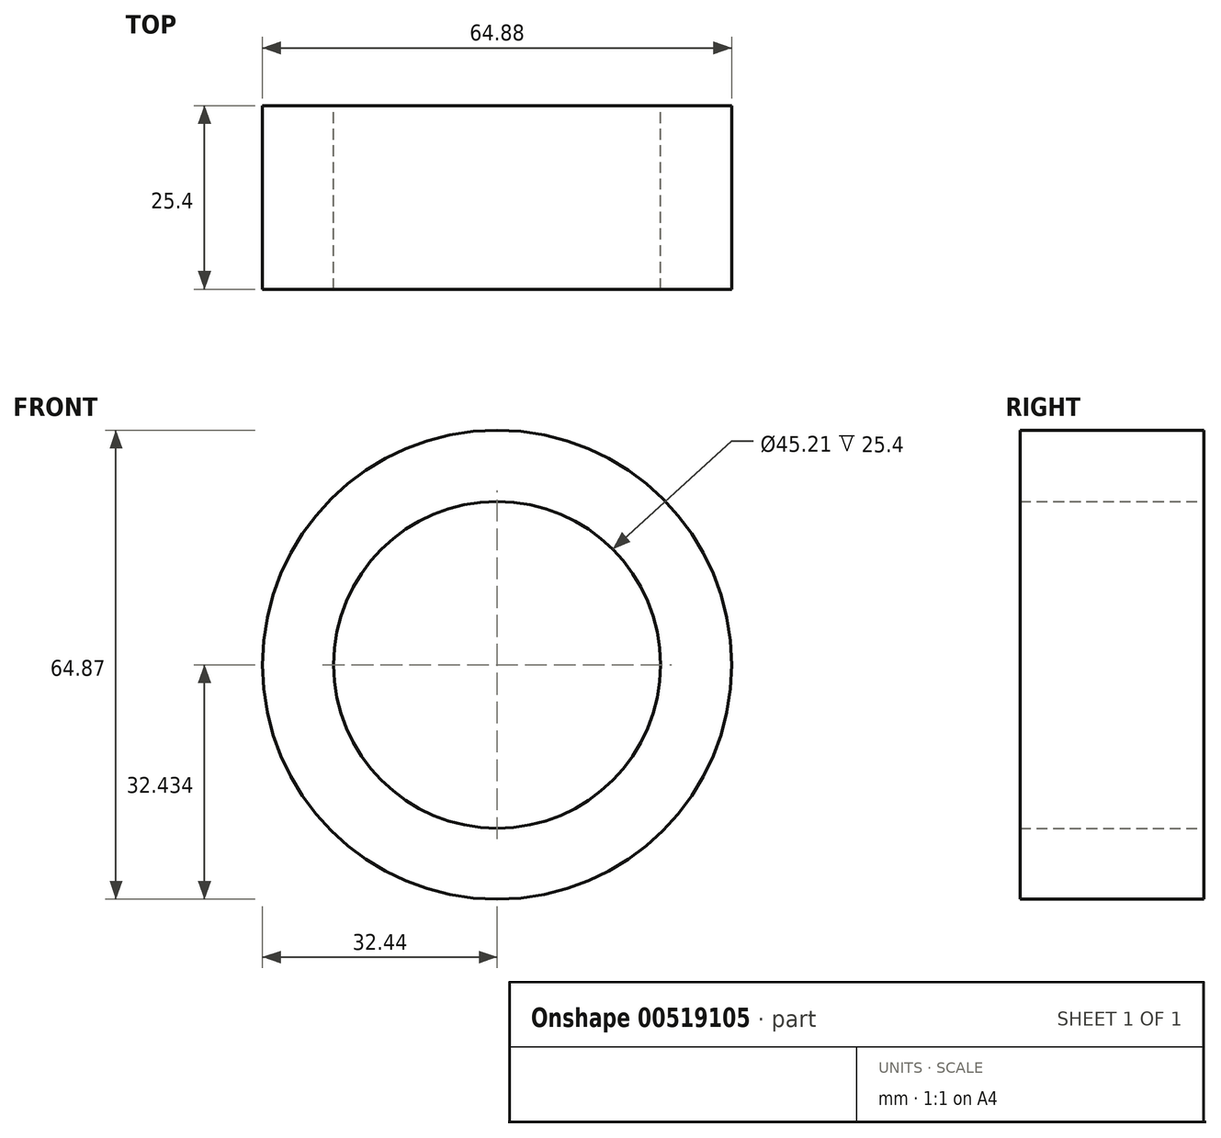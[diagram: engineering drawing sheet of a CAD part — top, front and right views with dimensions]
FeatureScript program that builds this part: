
annotation { "Feature Type Name" : "Feature", "Feature Type Description" : "" }
export const myFeature = defineFeature(function(context is Context, id is Id, definition is map)
    precondition{}
    {
        {
            var Q0;
            Q0=qCreatedBy(makeId("Front.planeOp"),FACE);
            var sketch = newSketch(context, id + "F0", { "sketchPlane" : qUnion([Q0])});
            skLineSegment(sketch, "E0.bottom", {"start": v(32.36, -50.06) * mm, "end": v(-32.36, -50.06) * mm});
            skLineSegment(sketch, "E0.top", {"start": v(32.36, 50.06) * mm, "end": v(-32.36, 50.06) * mm});
            skLineSegment(sketch, "E0.left", {"start": v(32.36, -50.06) * mm, "end": v(32.36, 50.06) * mm});
            skLineSegment(sketch, "E0.right", {"start": v(-32.36, -50.06) * mm, "end": v(-32.36, 50.06) * mm});
            skPoint(sketch, "E0.middle", {"position": v(0, 0) * mm});
            skCircle(sketch, "E1", {"center": v(0, 50.06) * mm, "radius": 32.44 * mm});
            skCircle(sketch, "E2", {"center": v(0, 50.06) * mm, "radius": 22.6 * mm});
            skSolve(sketch);
        }
        {
            var Q0;
            {var subQ1=sQuery(id+"F0.wireOp",EDGE,"E0.top");var subQ5=sQuery(id+"F0.wireOp",EDGE,"E0.left");var subQ6=makeQuery(id+"F0.imprint","INTERSECT",VERTEX,{"derivedFrom":[subQ1,subQ5]});Q0=makeQuery(id+"F0.imprint","IMPRINT",FACE,{"disambiguationData":[TD([[makeQuery(id+"F0.imprint","IMPRINT",EDGE,{"disambiguationData":[TD([[subQ6,-1.0]])],"derivedFrom":subQ1}),-1.0]])]});}
            var Q1;
            {var subQ1=sQuery(id+"F0.wireOp",EDGE,"E0.top");var subQ5=sQuery(id+"F0.wireOp",EDGE,"E0.left");var subQ6=makeQuery(id+"F0.imprint","INTERSECT",VERTEX,{"derivedFrom":[subQ1,subQ5]});Q1=makeQuery(id+"F0.imprint","IMPRINT",FACE,{"disambiguationData":[TD([[makeQuery(id+"F0.imprint","IMPRINT",EDGE,{"disambiguationData":[TD([[subQ6,-1.0]])],"derivedFrom":subQ1}),1.0]])]});}
            extrude(context, id + "F1", {"entities" : qUnion([Q0, Q1]), "depth" : 25.4 * mm});
        }
    });
